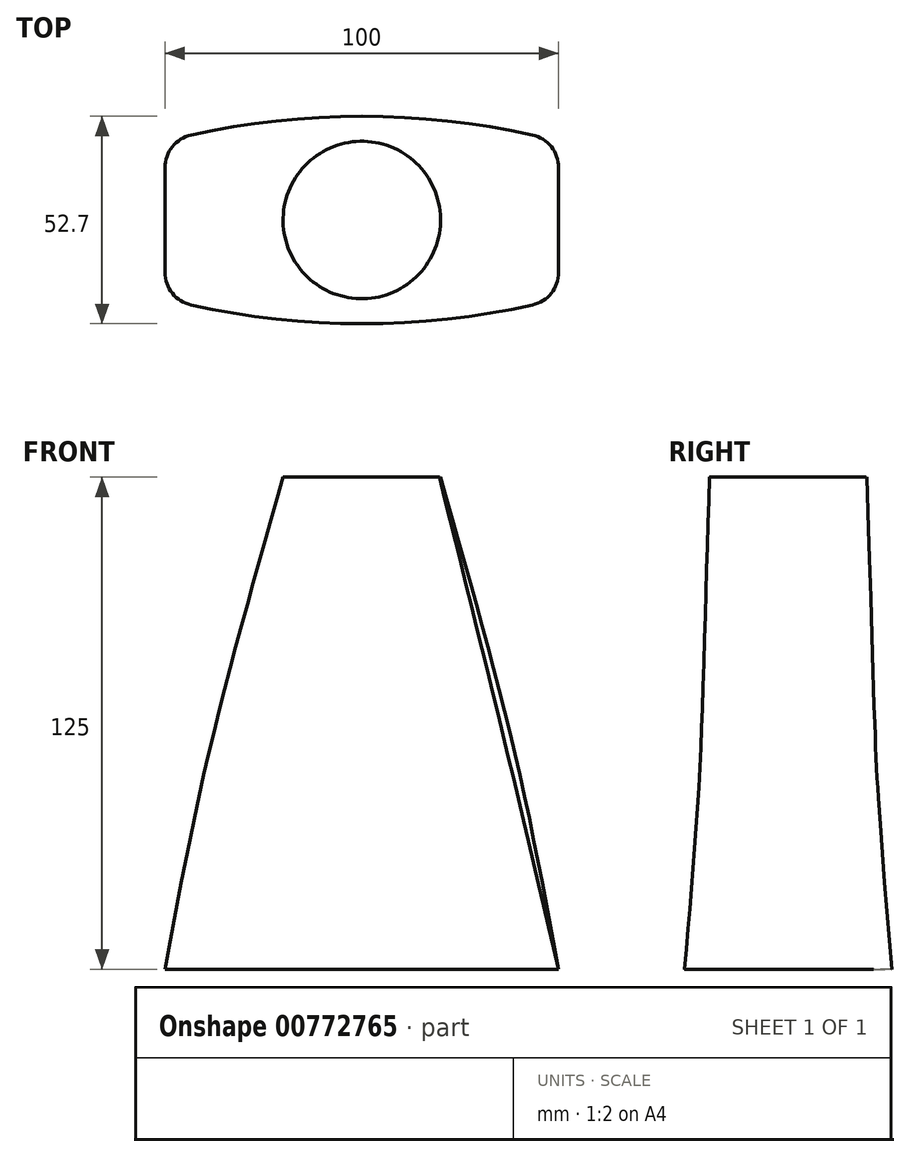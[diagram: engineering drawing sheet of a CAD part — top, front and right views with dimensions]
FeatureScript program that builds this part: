
annotation { "Feature Type Name" : "Feature", "Feature Type Description" : "" }
export const myFeature = defineFeature(function(context is Context, id is Id, definition is map)
    precondition{}
    {
        {
            var Q0;
            Q0=qCreatedBy(makeId("Top.planeOp"),FACE);
            var sketch = newSketch(context, id + "F0", { "sketchPlane" : qUnion([Q0])});
            skLineSegment(sketch, "E0.bottom", {"start": v(50, -20) * mm, "end": v(-50, -20) * mm, "construction": true});
            skLineSegment(sketch, "E0.top", {"start": v(50, 20) * mm, "end": v(-50, 20) * mm, "construction": true});
            skLineSegment(sketch, "E0.left", {"start": v(50, -13.3) * mm, "end": v(50, 13.3) * mm});
            skLineSegment(sketch, "E0.right", {"start": v(-50, -13.3) * mm, "end": v(-50, 13.3) * mm});
            skPoint(sketch, "E0.middle", {"position": v(0, 0) * mm});
            skArc(sketch, "E1", {"start": v(43.34, 21.6) * mm, "mid": v(0, 26.35) * mm, "end": v(-43.34, 21.6) * mm});
            skArc(sketch, "E2", {"start": v(-43.34, -21.6) * mm, "mid": v(0, -26.35) * mm, "end": v(43.34, -21.6) * mm});
            skPoint(sketch, "E3.visualSharp", {"position": v(-50, 20) * mm});
            skArc(sketch, "E3.filletArc", {"start": v(-43.34, 21.6) * mm, "mid": v(-48.13, 18.62) * mm, "end": v(-50, 13.3) * mm});
            skPoint(sketch, "E4.visualSharp", {"position": v(-50, -20) * mm});
            skArc(sketch, "E4.filletArc", {"start": v(-50, -13.3) * mm, "mid": v(-48.13, -18.62) * mm, "end": v(-43.34, -21.6) * mm});
            skPoint(sketch, "E5.visualSharp", {"position": v(50, -20) * mm});
            skArc(sketch, "E5.filletArc", {"start": v(43.34, -21.6) * mm, "mid": v(48.13, -18.62) * mm, "end": v(50, -13.3) * mm});
            skPoint(sketch, "E6.visualSharp", {"position": v(50, 20) * mm});
            skArc(sketch, "E6.filletArc", {"start": v(50, 13.3) * mm, "mid": v(48.13, 18.62) * mm, "end": v(43.34, 21.6) * mm});
            skSolve(sketch);
        }
        {
            var Q0;
            Q0=qCreatedBy(makeId("Top.planeOp"),FACE);
            cPlane(context, id + "F1", {"entities" : qUnion([Q0]), "cplaneType" : CPlaneType.OFFSET, "offset" : 50 * mm, "width" : 150 * mm, "height" : 150 * mm});
        }
        {
            var Q0;
            Q0=qCreatedBy(id+"F1.planeOp",FACE);
            var sketch = newSketch(context, id + "F2", { "sketchPlane" : qUnion([Q0])});
            skEllipse(sketch, "E7", {"center": v(0, 0) * mm, "majorRadius": 40 * mm, "minorRadius": 22.5 * mm, "majorAxis": v(-1, 0)});
            skSolve(sketch);
        }
        {
            var Q0;
            Q0=qCreatedBy(makeId("Top.planeOp"),FACE);
            cPlane(context, id + "F3", {"entities" : qUnion([Q0]), "cplaneType" : CPlaneType.OFFSET, "offset" : 125 * mm, "width" : 150 * mm, "height" : 150 * mm});
        }
        {
            var Q0;
            Q0=qCreatedBy(id+"F3.planeOp",FACE);
            var sketch = newSketch(context, id + "F4", { "sketchPlane" : qUnion([Q0])});
            skCircle(sketch, "E8", {"center": v(0, 0) * mm, "radius": 20 * mm});
            skSolve(sketch);
        }
        {
            var Q0;
            Q0 = qSketchRegion(id + "F0", true);
            var Q1;
            Q1 = qSketchRegion(id + "F2", true);
            var Q2;
            Q2 = qSketchRegion(id + "F4", true);
            loft(context, id + "F5", {"sheetProfilesArray" : [{ "sheetProfileEntities" : qUnion([Q0]) }, { "sheetProfileEntities" : qUnion([Q1]) }, { "sheetProfileEntities" : qUnion([Q2]) }]});
        }
    });
